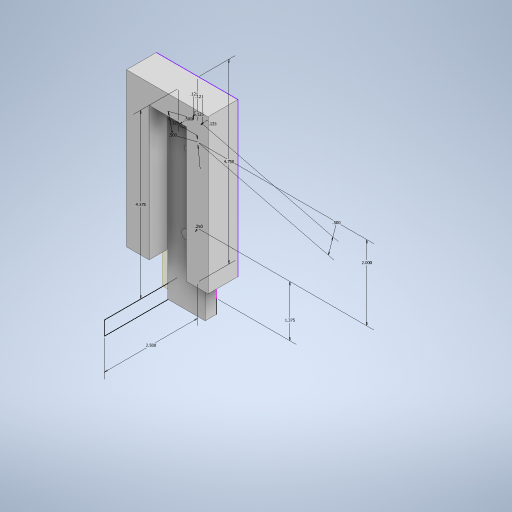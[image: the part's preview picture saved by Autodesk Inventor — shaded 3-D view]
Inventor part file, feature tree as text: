
AUTODESK INVENTOR PART (.ipt)
format: ipt  version: 2023 (Build 270158000, 158)  size: 275,968 bytes
history: native  units: in
note: dims shown in document units (in); Inventor stores cm internally (conversion verified against a paired STEP export)
features: sketch x2, extrude x2, plane x1
ambient origin geometry x8: Origin, YZ Plane, XZ Plane, XY Plane, X Axis, Y Axis, Z Axis, Center Point
bodies: Body1 (feature_tree)
feature tree (5):
  sketch  "Sketch1"  dims[d0=4.375in d1=0.5in]
  plane  "Work Plane1"
  sketch  "Sketch2"  dims[d2=4.75in d3=2.5in d7=0.25in d8=0.125in d9=1.375in d10=2.0in d11=0.125in d12=0.5in d17=0.125in d18=0.5in d22=0.1213in d23=0.1213in d30=0.3in d31=0.0in d32=0.8in d33=0.0in]
  extrude  "Extrusion4"  Depth=0.5in
  extrude  "Extrusion5"  Depth=0.8in
